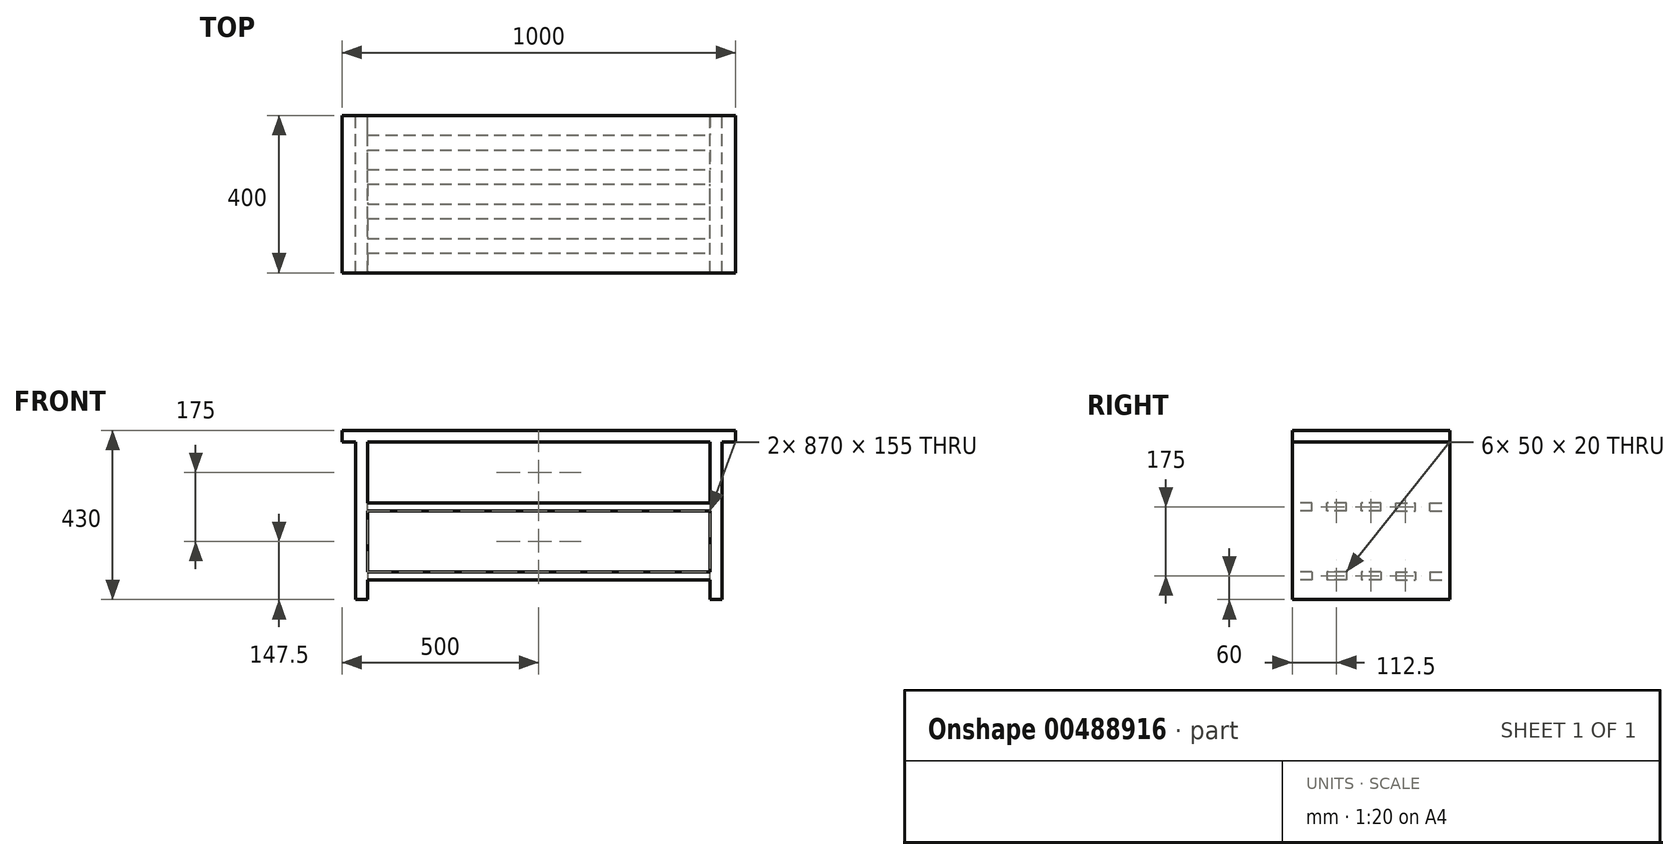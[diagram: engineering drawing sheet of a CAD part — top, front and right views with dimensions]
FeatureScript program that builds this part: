
annotation { "Feature Type Name" : "Feature", "Feature Type Description" : "" }
export const myFeature = defineFeature(function(context is Context, id is Id, definition is map)
    precondition{}
    {
        {
            var Q0;
            Q0=qCreatedBy(makeId("Top.planeOp"),FACE);
            var sketch = newSketch(context, id + "F0", { "sketchPlane" : qUnion([Q0])});
            skLineSegment(sketch, "E0.bottom", {"start": v(500, 200) * mm, "end": v(-500, 200) * mm});
            skLineSegment(sketch, "E0.top", {"start": v(500, -200) * mm, "end": v(-500, -200) * mm});
            skLineSegment(sketch, "E0.left", {"start": v(500, 200) * mm, "end": v(500, -200) * mm});
            skLineSegment(sketch, "E0.right", {"start": v(-500, 200) * mm, "end": v(-500, -200) * mm});
            skPoint(sketch, "E0.middle", {"position": v(0, 0) * mm});
            skSolve(sketch);
        }
        {
            var Q0;
            Q0 = qSketchRegion(id + "F0", true);
            extrude(context, id + "F1", {"entities" : qUnion([Q0]), "oppositeDirection" : true, "depth" : 30 * mm});
        }
        {
            var Q0;
            Q0=makeQuery(id+"F1.opExtrude","CAP_FACE",FACE,{"disambiguationData":[OSD([sQuery(id+"F0.wireOp",EDGE,"E0.bottom"),sQuery(id+"F0.wireOp",EDGE,"E0.top"),sQuery(id+"F0.wireOp",EDGE,"E0.left"),sQuery(id+"F0.wireOp",EDGE,"E0.right")])],"isStart":false});
            var sketch = newSketch(context, id + "F2", { "sketchPlane" : qUnion([Q0])});
            skLineSegment(sketch, "E1.bottom", {"start": v(-435, 200) * mm, "end": v(-465, 200) * mm});
            skLineSegment(sketch, "E1.top", {"start": v(-435, -200) * mm, "end": v(-465, -200) * mm});
            skLineSegment(sketch, "E1.left", {"start": v(-435, 200) * mm, "end": v(-435, -200) * mm});
            skLineSegment(sketch, "E1.right", {"start": v(-465, 200) * mm, "end": v(-465, -200) * mm});
            skPoint(sketch, "E1.middle", {"position": v(-450, 0) * mm});
            skLineSegment(sketch, "E2", {"start": v(0, 0) * mm, "end": v(0, -200) * mm, "construction": true});
            skLineSegment(sketch, "E3.MirrorCS", {"start": v(435, 200) * mm, "end": v(465, 200) * mm});
            skLineSegment(sketch, "E4.MirrorCS", {"start": v(435, -200) * mm, "end": v(465, -200) * mm});
            skLineSegment(sketch, "E5.MirrorCS", {"start": v(465, 200) * mm, "end": v(465, -200) * mm});
            skLineSegment(sketch, "E6.MirrorCS", {"start": v(435, 200) * mm, "end": v(435, -200) * mm});
            skSolve(sketch);
        }
        {
            var Q0;
            Q0=makeQuery(id+"F2.imprint","IMPRINT",FACE,{"disambiguationData":[TD([[makeQuery(id+"F2.imprint","IMPRINT",EDGE,{"derivedFrom":sQuery(id+"F2.wireOp",EDGE,"E1.bottom")}),1.0]])]});
            var Q1;
            Q1=makeQuery(id+"F2.imprint","IMPRINT",FACE,{"disambiguationData":[TD([[makeQuery(id+"F2.imprint","IMPRINT",EDGE,{"derivedFrom":sQuery(id+"F2.wireOp",EDGE,"E3.MirrorCS")}),1.0]])]});
            extrude(context, id + "F3", {"entities" : qUnion([Q0, Q1]), "operationType" : NewBodyOperationType.ADD, "depth" : 400 * mm});
        }
        {
            var Q0;
            Q0=makeQuery(id+"F3.opExtrude","SWEPT_FACE",FACE,{"disambiguationData":[OSD([sQuery(id+"F2.wireOp",EDGE,"E6.MirrorCS")])]});
            var sketch = newSketch(context, id + "F4", { "sketchPlane" : qUnion([Q0])});
            skLineSegment(sketch, "E7.bottom", {"start": v(25, -380) * mm, "end": v(-25, -380) * mm});
            skLineSegment(sketch, "E7.top", {"start": v(25, -360) * mm, "end": v(-25, -360) * mm});
            skLineSegment(sketch, "E7.left", {"start": v(25, -380) * mm, "end": v(25, -360) * mm});
            skLineSegment(sketch, "E7.right", {"start": v(-25, -380) * mm, "end": v(-25, -360) * mm});
            skPoint(sketch, "E7.middle", {"position": v(0, -370) * mm});
            skPoint(sketch, "E7.middle.positionSnap0", {"position": v(0, -430) * mm});
            skPoint(sketch, "E7.centerSnap0", {"position": v(0, -430) * mm});
            skLineSegment(sketch, "E8.bottom", {"start": v(112.5, -380) * mm, "end": v(62.5, -380) * mm});
            skLineSegment(sketch, "E8.top", {"start": v(112.5, -360) * mm, "end": v(62.5, -360) * mm});
            skLineSegment(sketch, "E8.left", {"start": v(112.5, -380) * mm, "end": v(112.5, -360) * mm});
            skLineSegment(sketch, "E8.right", {"start": v(62.5, -380) * mm, "end": v(62.5, -360) * mm});
            skPoint(sketch, "E8.middle", {"position": v(87.5, -370) * mm});
            skLineSegment(sketch, "E9.bottom", {"start": v(200, -380) * mm, "end": v(150, -380) * mm});
            skLineSegment(sketch, "E9.top", {"start": v(200, -360) * mm, "end": v(150, -360) * mm});
            skLineSegment(sketch, "E9.left", {"start": v(200, -380) * mm, "end": v(200, -360) * mm});
            skLineSegment(sketch, "E9.right", {"start": v(150, -380) * mm, "end": v(150, -360) * mm});
            skPoint(sketch, "E9.middle", {"position": v(175, -370) * mm});
            skPoint(sketch, "E9.middle.positionSnap0", {"position": v(112.5, -370) * mm});
            skPoint(sketch, "E9.centerSnap0", {"position": v(112.5, -370) * mm});
            skLineSegment(sketch, "E10", {"start": v(0, -430) * mm, "end": v(0, -370) * mm, "construction": true});
            skLineSegment(sketch, "E11.MirrorCS", {"start": v(-200, -380) * mm, "end": v(-150, -380) * mm});
            skLineSegment(sketch, "E12.MirrorCS", {"start": v(-200, -380) * mm, "end": v(-200, -360) * mm});
            skLineSegment(sketch, "E13.MirrorCS", {"start": v(-200, -360) * mm, "end": v(-150, -360) * mm});
            skLineSegment(sketch, "E14.MirrorCS", {"start": v(-150, -380) * mm, "end": v(-150, -360) * mm});
            skLineSegment(sketch, "E15.MirrorCS", {"start": v(-112.5, -380) * mm, "end": v(-112.5, -360) * mm});
            skLineSegment(sketch, "E16.MirrorCS", {"start": v(-112.5, -360) * mm, "end": v(-62.5, -360) * mm});
            skLineSegment(sketch, "E17.MirrorCS", {"start": v(-112.5, -380) * mm, "end": v(-62.5, -380) * mm});
            skLineSegment(sketch, "E18.MirrorCS", {"start": v(-62.5, -380) * mm, "end": v(-62.5, -360) * mm});
            skLineSegment(sketch, "E19", {"start": v(0, -370) * mm, "end": v(0, -282.5) * mm, "construction": true});
            skLineSegment(sketch, "E20", {"start": v(0, -282.5) * mm, "end": v(-200, -282.5) * mm, "construction": true});
            skLineSegment(sketch, "E21.MirrorCS", {"start": v(-200, -185) * mm, "end": v(-200, -205) * mm});
            skLineSegment(sketch, "E22.MirrorCS", {"start": v(-200, -185) * mm, "end": v(-150, -185) * mm});
            skLineSegment(sketch, "E23.MirrorCS", {"start": v(-200, -205) * mm, "end": v(-150, -205) * mm});
            skLineSegment(sketch, "E24.MirrorCS", {"start": v(-150, -185) * mm, "end": v(-150, -205) * mm});
            skLineSegment(sketch, "E25.MirrorCS", {"start": v(-112.5, -205) * mm, "end": v(-62.5, -205) * mm});
            skLineSegment(sketch, "E26.MirrorCS", {"start": v(-112.5, -185) * mm, "end": v(-112.5, -205) * mm});
            skLineSegment(sketch, "E27.MirrorCS", {"start": v(-112.5, -185) * mm, "end": v(-62.5, -185) * mm});
            skLineSegment(sketch, "E28.MirrorCS", {"start": v(-62.5, -185) * mm, "end": v(-62.5, -205) * mm});
            skLineSegment(sketch, "E29.MirrorCS", {"start": v(-25, -185) * mm, "end": v(-25, -205) * mm});
            skLineSegment(sketch, "E30.MirrorCS", {"start": v(25, -185) * mm, "end": v(-25, -185) * mm});
            skLineSegment(sketch, "E31.MirrorCS", {"start": v(25, -205) * mm, "end": v(-25, -205) * mm});
            skLineSegment(sketch, "E32.MirrorCS", {"start": v(25, -185) * mm, "end": v(25, -205) * mm});
            skLineSegment(sketch, "E33.MirrorCS", {"start": v(112.5, -185) * mm, "end": v(62.5, -185) * mm});
            skLineSegment(sketch, "E34.MirrorCS", {"start": v(62.5, -185) * mm, "end": v(62.5, -205) * mm});
            skLineSegment(sketch, "E35.MirrorCS", {"start": v(112.5, -205) * mm, "end": v(62.5, -205) * mm});
            skLineSegment(sketch, "E36.MirrorCS", {"start": v(112.5, -185) * mm, "end": v(112.5, -205) * mm});
            skLineSegment(sketch, "E37.MirrorCS", {"start": v(150, -185) * mm, "end": v(150, -205) * mm});
            skLineSegment(sketch, "E38.MirrorCS", {"start": v(200, -185) * mm, "end": v(150, -185) * mm});
            skLineSegment(sketch, "E39.MirrorCS", {"start": v(200, -185) * mm, "end": v(200, -205) * mm});
            skLineSegment(sketch, "E40.MirrorCS", {"start": v(200, -205) * mm, "end": v(150, -205) * mm});
            skSolve(sketch);
        }
        {
            var Q0;
            Q0=makeQuery(id+"F4.imprint","IMPRINT",FACE,{"disambiguationData":[TD([[makeQuery(id+"F4.imprint","IMPRINT",EDGE,{"derivedFrom":sQuery(id+"F4.wireOp",EDGE,"E21.MirrorCS")}),-1.0]])]});
            var Q1;
            Q1=makeQuery(id+"F4.imprint","IMPRINT",FACE,{"disambiguationData":[TD([[makeQuery(id+"F4.imprint","IMPRINT",EDGE,{"derivedFrom":sQuery(id+"F4.wireOp",EDGE,"E25.MirrorCS")}),1.0]])]});
            var Q2;
            Q2=makeQuery(id+"F4.imprint","IMPRINT",FACE,{"disambiguationData":[TD([[makeQuery(id+"F4.imprint","IMPRINT",EDGE,{"derivedFrom":sQuery(id+"F4.wireOp",EDGE,"E29.MirrorCS")}),1.0]])]});
            var Q3;
            Q3=makeQuery(id+"F4.imprint","IMPRINT",FACE,{"disambiguationData":[TD([[makeQuery(id+"F4.imprint","IMPRINT",EDGE,{"derivedFrom":sQuery(id+"F4.wireOp",EDGE,"E33.MirrorCS")}),1.0]])]});
            var Q4;
            Q4=makeQuery(id+"F4.imprint","IMPRINT",FACE,{"disambiguationData":[TD([[makeQuery(id+"F4.imprint","IMPRINT",EDGE,{"derivedFrom":sQuery(id+"F4.wireOp",EDGE,"E37.MirrorCS")}),1.0]])]});
            var Q5;
            Q5=makeQuery(id+"F4.imprint","IMPRINT",FACE,{"disambiguationData":[TD([[makeQuery(id+"F4.imprint","IMPRINT",EDGE,{"derivedFrom":sQuery(id+"F4.wireOp",EDGE,"E9.bottom")}),-1.0]])]});
            var Q6;
            Q6=makeQuery(id+"F4.imprint","IMPRINT",FACE,{"disambiguationData":[TD([[makeQuery(id+"F4.imprint","IMPRINT",EDGE,{"derivedFrom":sQuery(id+"F4.wireOp",EDGE,"E8.bottom")}),-1.0]])]});
            var Q7;
            Q7=makeQuery(id+"F4.imprint","IMPRINT",FACE,{"disambiguationData":[TD([[makeQuery(id+"F4.imprint","IMPRINT",EDGE,{"derivedFrom":sQuery(id+"F4.wireOp",EDGE,"E7.bottom")}),-1.0]])]});
            var Q8;
            Q8=makeQuery(id+"F4.imprint","IMPRINT",FACE,{"disambiguationData":[TD([[makeQuery(id+"F4.imprint","IMPRINT",EDGE,{"derivedFrom":sQuery(id+"F4.wireOp",EDGE,"E15.MirrorCS")}),-1.0]])]});
            var Q9;
            Q9=makeQuery(id+"F4.imprint","IMPRINT",FACE,{"disambiguationData":[TD([[makeQuery(id+"F4.imprint","IMPRINT",EDGE,{"derivedFrom":sQuery(id+"F4.wireOp",EDGE,"E11.MirrorCS")}),1.0]])]});
            var Q10;
            Q10=makeQuery(id+"F3.opExtrude","SWEPT_FACE",FACE,{"disambiguationData":[OSD([sQuery(id+"F2.wireOp",EDGE,"E1.left")])]});
            extrude(context, id + "F5", {"entities" : qUnion([Q0, Q1, Q2, Q3, Q4, Q5, Q6, Q7, Q8, Q9]), "operationType" : NewBodyOperationType.ADD, "endBound" : BoundingType.UP_TO_SURFACE, "endBoundEntityFace" : qUnion([Q10]), "depth" : 25 * mm});
        }
    });
